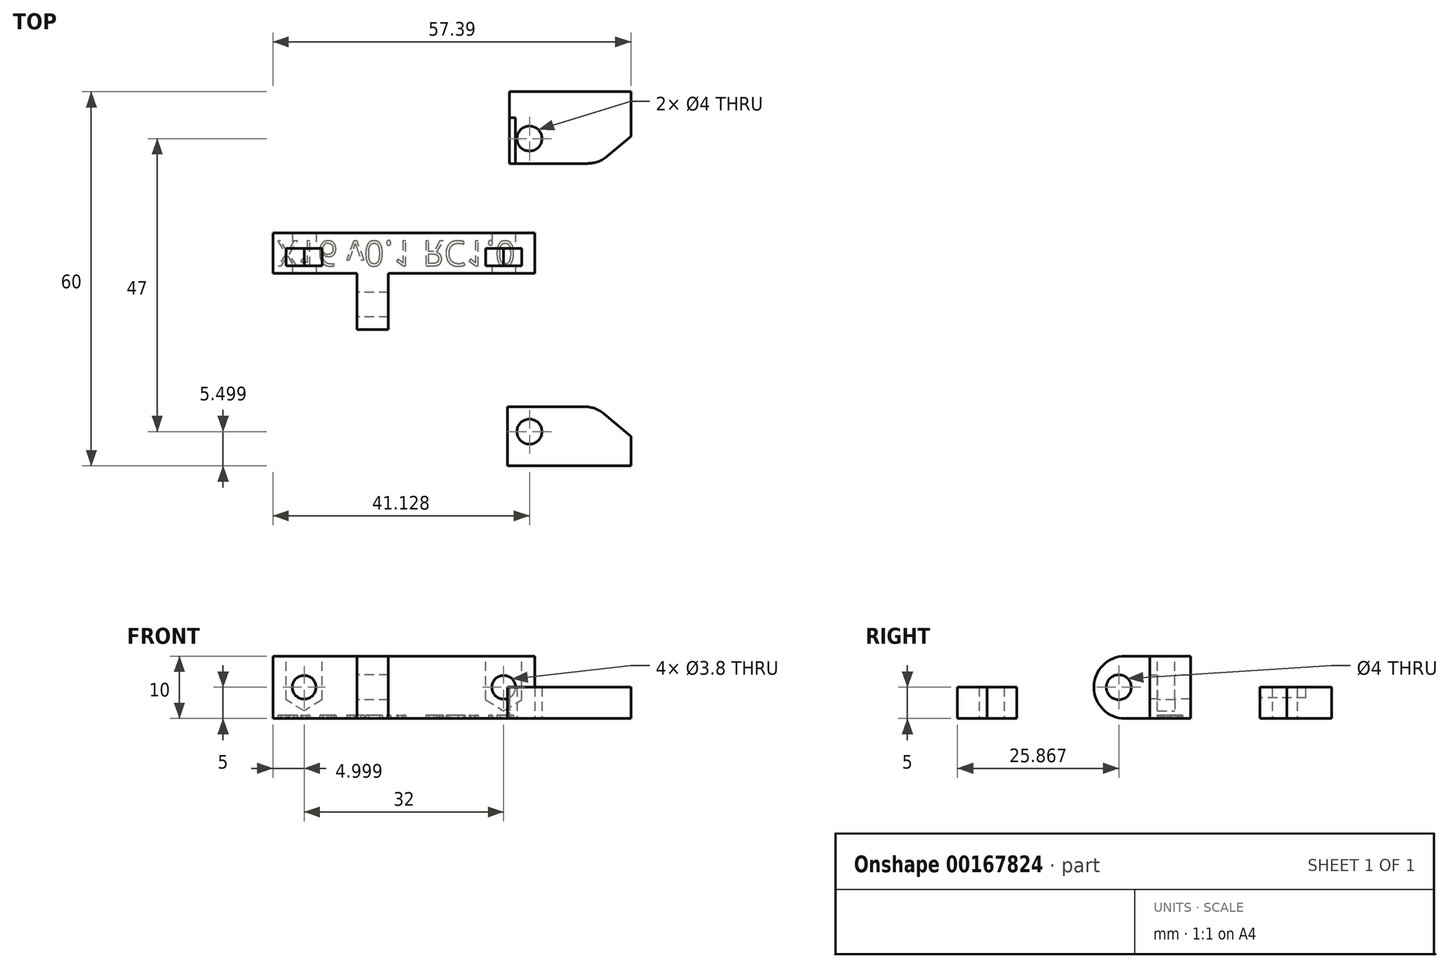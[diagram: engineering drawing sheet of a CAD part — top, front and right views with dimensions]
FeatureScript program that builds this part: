
annotation { "Feature Type Name" : "Feature", "Feature Type Description" : "" }
export const myFeature = defineFeature(function(context is Context, id is Id, definition is map)
    precondition{}
    {
        {
            var Q0;
            Q0=qCreatedBy(makeId("Top.planeOp"),FACE);
            var sketch = newSketch(context, id + "F0", { "sketchPlane" : qUnion([Q0])});
            skLineSegment(sketch, "E0.bottom", {"start": v(-19, 16.47) * mm, "end": v(-6.51, 16.47) * mm});
            skLineSegment(sketch, "E0.top", {"start": v(-19, 27.97) * mm, "end": v(0.47, 27.97) * mm});
            skLineSegment(sketch, "E0.left", {"start": v(-19, 16.47) * mm, "end": v(-19, 27.97) * mm});
            skLineSegment(sketch, "E0.right", {"start": v(0.47, 16.47) * mm, "end": v(0.47, 27.97) * mm});
            skLineSegment(sketch, "E1.bottom", {"start": v(-19.3, -32.03) * mm, "end": v(0.47, -32.03) * mm});
            skLineSegment(sketch, "E1.top", {"start": v(-19.3, -22.53) * mm, "end": v(-7.01, -22.53) * mm});
            skLineSegment(sketch, "E1.left", {"start": v(-19.3, -32.03) * mm, "end": v(-19.3, -22.53) * mm});
            skLineSegment(sketch, "E1.right", {"start": v(0.47, -32.03) * mm, "end": v(0.47, -22.53) * mm});
            skCircle(sketch, "E2", {"center": v(-15.8, 20.47) * mm, "radius": 2 * mm});
            skCircle(sketch, "E3", {"center": v(-15.8, -26.53) * mm, "radius": 2 * mm});
            skLineSegment(sketch, "E4", {"start": v(0.47, -27.28) * mm, "end": v(-3.8, -23.7) * mm});
            skLineSegment(sketch, "E5", {"start": v(-3.3, 17.64) * mm, "end": v(0.47, 20.8) * mm});
            skPoint(sketch, "E6.visualSharp", {"position": v(-5.2, -22.53) * mm});
            skArc(sketch, "E6.filletArc", {"start": v(-3.8, -23.7) * mm, "mid": v(-5.3, -22.83) * mm, "end": v(-7.01, -22.53) * mm});
            skPoint(sketch, "E7.visualSharp", {"position": v(-4.7, 16.47) * mm});
            skArc(sketch, "E7.filletArc", {"start": v(-6.51, 16.47) * mm, "mid": v(-4.8, 16.77) * mm, "end": v(-3.3, 17.64) * mm});
            skSolve(sketch);
        }
        {
            var Q0;
            Q0 = qSketchRegion(id + "F0", true);
            extrude(context, id + "F1", {"entities" : qUnion([Q0]), "depth" : 5 * mm});
        }
        {
            var Q0;
            Q0=qCreatedBy(makeId("Top.planeOp"),FACE);
            var sketch = newSketch(context, id + "F2", { "sketchPlane" : qUnion([Q0])});
            skLineSegment(sketch, "E8.bottom", {"start": v(-56.92, 5.34) * mm, "end": v(-14.92, 5.34) * mm});
            skLineSegment(sketch, "E8.top", {"start": v(-56.92, -1.16) * mm, "end": v(-14.92, -1.16) * mm});
            skLineSegment(sketch, "E8.left", {"start": v(-56.92, 5.34) * mm, "end": v(-56.92, -1.16) * mm});
            skLineSegment(sketch, "E8.right", {"start": v(-14.92, 5.34) * mm, "end": v(-14.92, -1.16) * mm});
            skLineSegment(sketch, "E9.bottom", {"start": v(-38.42, -1.16) * mm, "end": v(-43.42, -1.16) * mm});
            skLineSegment(sketch, "E9.top", {"start": v(-38.42, -10.16) * mm, "end": v(-43.42, -10.16) * mm});
            skLineSegment(sketch, "E9.left", {"start": v(-38.42, -1.16) * mm, "end": v(-38.42, -10.16) * mm});
            skLineSegment(sketch, "E9.right", {"start": v(-43.42, -1.16) * mm, "end": v(-43.42, -10.16) * mm});
            skSolve(sketch);
        }
        {
            var Q0;
            Q0 = qSketchRegion(id + "F2", true);
            extrude(context, id + "F3", {"entities" : qUnion([Q0]), "depth" : 10 * mm});
        }
        {
            var Q0;
            Q0=makeQuery(id+"F3.opExtrude","CAP_EDGE",EDGE,{"disambiguationData":[OSD([sQuery(id+"F2.wireOp",EDGE,"E9.top")])],"isStart":false});
            var Q1;
            Q1=makeQuery(id+"F3.opExtrude","CAP_EDGE",EDGE,{"disambiguationData":[OSD([sQuery(id+"F2.wireOp",EDGE,"E9.top")])],"isStart":true});
            fillet(context, id + "F4", {"entities" : qUnion([Q0, Q1]), "radius" : 5 * mm, "tangentPropagation" : true, "allowEdgeOverflow" : false});
        }
        {
            var Q0;
            Q0=makeQuery(id+"F3.opExtrude","SWEPT_FACE",FACE,{"disambiguationData":[OSD([sQuery(id+"F2.wireOp",EDGE,"E9.right")])]});
            var sketch = newSketch(context, id + "F5", { "sketchPlane" : qUnion([Q0])});
            skCircle(sketch, "E10", {"center": v(6.16, 5) * mm, "radius": 2 * mm});
            skPoint(sketch, "E10.centerSnap0", {"position": v(10.16, 5) * mm});
            skSolve(sketch);
        }
        {
            var Q0;
            Q0 = qSketchRegion(id + "F5", true);
            extrude(context, id + "F6", {"entities" : qUnion([Q0]), "operationType" : NewBodyOperationType.REMOVE, "oppositeDirection" : true, "depth" : 25 * mm});
        }
        {
            var Q0;
            {var subQ0=sQuery(id+"F2.wireOp",EDGE,"E8.top");Q0=makeQuery(id+"F3.opExtrude","SWEPT_FACE",FACE,{"disambiguationData":[OSD([subQ0]),TDD([makeQuery(id+"F2.imprint","IMPRINT",EDGE,{"disambiguationData":[TD([[makeQuery(id+"F2.imprint","INTERSECT",VERTEX,{"derivedFrom":[subQ0,sQuery(id+"F2.wireOp",EDGE,"E8.left")]}),-1.0]])],"derivedFrom":subQ0})])]});}
            var sketch = newSketch(context, id + "F7", { "sketchPlane" : qUnion([Q0])});
            skCircle(sketch, "E11", {"center": v(-51.92, 5) * mm, "radius": 1.9 * mm});
            skPoint(sketch, "E11.centerSnap0", {"position": v(-56.92, 5) * mm});
            skPoint(sketch, "E12.0", {"position": v(-14.92, 5) * mm});
            skLineSegment(sketch, "E13", {"start": v(-14.92, 5) * mm, "end": v(-19.92, 5) * mm, "construction": true});
            skCircle(sketch, "E14", {"center": v(-19.92, 5) * mm, "radius": 1.9 * mm});
            skSolve(sketch);
        }
        {
            var Q0;
            Q0 = qSketchRegion(id + "F7", true);
            extrude(context, id + "F8", {"entities" : qUnion([Q0]), "operationType" : NewBodyOperationType.REMOVE, "oppositeDirection" : true, "depth" : 25 * mm});
        }
        {
            var Q0;
            Q0=makeQuery(id+"F3.opExtrude","CAP_FACE",FACE,{"disambiguationData":[OSD([sQuery(id+"F2.wireOp",EDGE,"E8.bottom"),sQuery(id+"F2.wireOp",EDGE,"E8.top"),sQuery(id+"F2.wireOp",EDGE,"E8.left"),sQuery(id+"F2.wireOp",EDGE,"E8.right"),sQuery(id+"F2.wireOp",EDGE,"E9.top"),sQuery(id+"F2.wireOp",EDGE,"E9.left"),sQuery(id+"F2.wireOp",EDGE,"E9.right")])],"isStart":false});
            var sketch = newSketch(context, id + "F9", { "sketchPlane" : qUnion([Q0])});
            skLineSegment(sketch, "E15.bottom", {"start": v(-22.82, 2.84) * mm, "end": v(-17.02, 2.84) * mm});
            skLineSegment(sketch, "E15.top", {"start": v(-22.82, 0.04) * mm, "end": v(-17.02, 0.04) * mm});
            skLineSegment(sketch, "E15.left", {"start": v(-22.82, 2.84) * mm, "end": v(-22.82, 0.04) * mm});
            skLineSegment(sketch, "E15.right", {"start": v(-17.02, 2.84) * mm, "end": v(-17.02, 0.04) * mm});
            skPoint(sketch, "E16", {"position": v(-19.92, 2.84) * mm});
            skLineSegment(sketch, "E17.bottom", {"start": v(-49.02, 2.84) * mm, "end": v(-54.82, 2.84) * mm});
            skLineSegment(sketch, "E17.top", {"start": v(-49.02, 0.04) * mm, "end": v(-54.82, 0.04) * mm});
            skLineSegment(sketch, "E17.left", {"start": v(-49.02, 2.84) * mm, "end": v(-49.02, 0.04) * mm});
            skLineSegment(sketch, "E17.right", {"start": v(-54.82, 2.84) * mm, "end": v(-54.82, 0.04) * mm});
            skPoint(sketch, "E18", {"position": v(-51.92, 2.84) * mm});
            skSolve(sketch);
        }
        {
            var Q0;
            Q0 = qSketchRegion(id + "F9", true);
            extrude(context, id + "F10", {"entities" : qUnion([Q0]), "operationType" : NewBodyOperationType.REMOVE, "oppositeDirection" : true, "depth" : 7 * mm});
        }
        {
            var Q0;
            Q0=makeQuery(id+"F10.boolean.opBoolean","COPY",FACE,{"derivedFrom":makeQuery(id+"F10.opExtrude","SWEPT_FACE",FACE,{"disambiguationData":[OSD([sQuery(id+"F9.wireOp",EDGE,"E17.bottom")])]})});
            var sketch = newSketch(context, id + "F11", { "sketchPlane" : qUnion([Q0])});
            skLineSegment(sketch, "E19", {"start": v(-54.82, 3) * mm, "end": v(-49.02, 3) * mm});
            skLineSegment(sketch, "E20", {"start": v(-49.02, 3) * mm, "end": v(-51.92, 1.23) * mm});
            skLineSegment(sketch, "E21", {"start": v(-51.92, 1.23) * mm, "end": v(-54.82, 3) * mm});
            skLineSegment(sketch, "E22.0", {"start": v(-22.82, 3) * mm, "end": v(-17.02, 3) * mm});
            skLineSegment(sketch, "E23", {"start": v(-22.82, 3) * mm, "end": v(-19.92, 1.23) * mm});
            skLineSegment(sketch, "E24", {"start": v(-19.92, 1.23) * mm, "end": v(-17.02, 3) * mm});
            skSolve(sketch);
        }
        {
            var Q0;
            Q0 = qSketchRegion(id + "F11", true);
            extrude(context, id + "F12", {"entities" : qUnion([Q0]), "operationType" : NewBodyOperationType.REMOVE, "depth" : 2.8 * mm});
        }
        {
            var Q0;
            Q0=makeQuery(id+"F3.opExtrude","CAP_FACE",FACE,{"disambiguationData":[OSD([sQuery(id+"F2.wireOp",EDGE,"E8.bottom"),sQuery(id+"F2.wireOp",EDGE,"E8.top"),sQuery(id+"F2.wireOp",EDGE,"E8.left"),sQuery(id+"F2.wireOp",EDGE,"E8.right"),sQuery(id+"F2.wireOp",EDGE,"E9.top"),sQuery(id+"F2.wireOp",EDGE,"E9.left"),sQuery(id+"F2.wireOp",EDGE,"E9.right")])],"isStart":true});
            var sketch = newSketch(context, id + "F13", { "sketchPlane" : qUnion([Q0])});
            skText(sketch, "E25", { "text": "X16 v0.1 RC1.0", "fontName": "OpenSans-Regular.ttf"});
            const initialGuessF13  = {"E25": [-0.0562, -0.00403, 1, 0, 0.00403]};
            skSetInitialGuess(sketch, initialGuessF13);
            skSolve(sketch);
        }
        {
            var Q0;
            Q0 = qSketchRegion(id + "F13", true);
            extrude(context, id + "F14", {"entities" : qUnion([Q0]), "operationType" : NewBodyOperationType.REMOVE, "oppositeDirection" : true, "depth" : .5 * mm});
        }
    });
